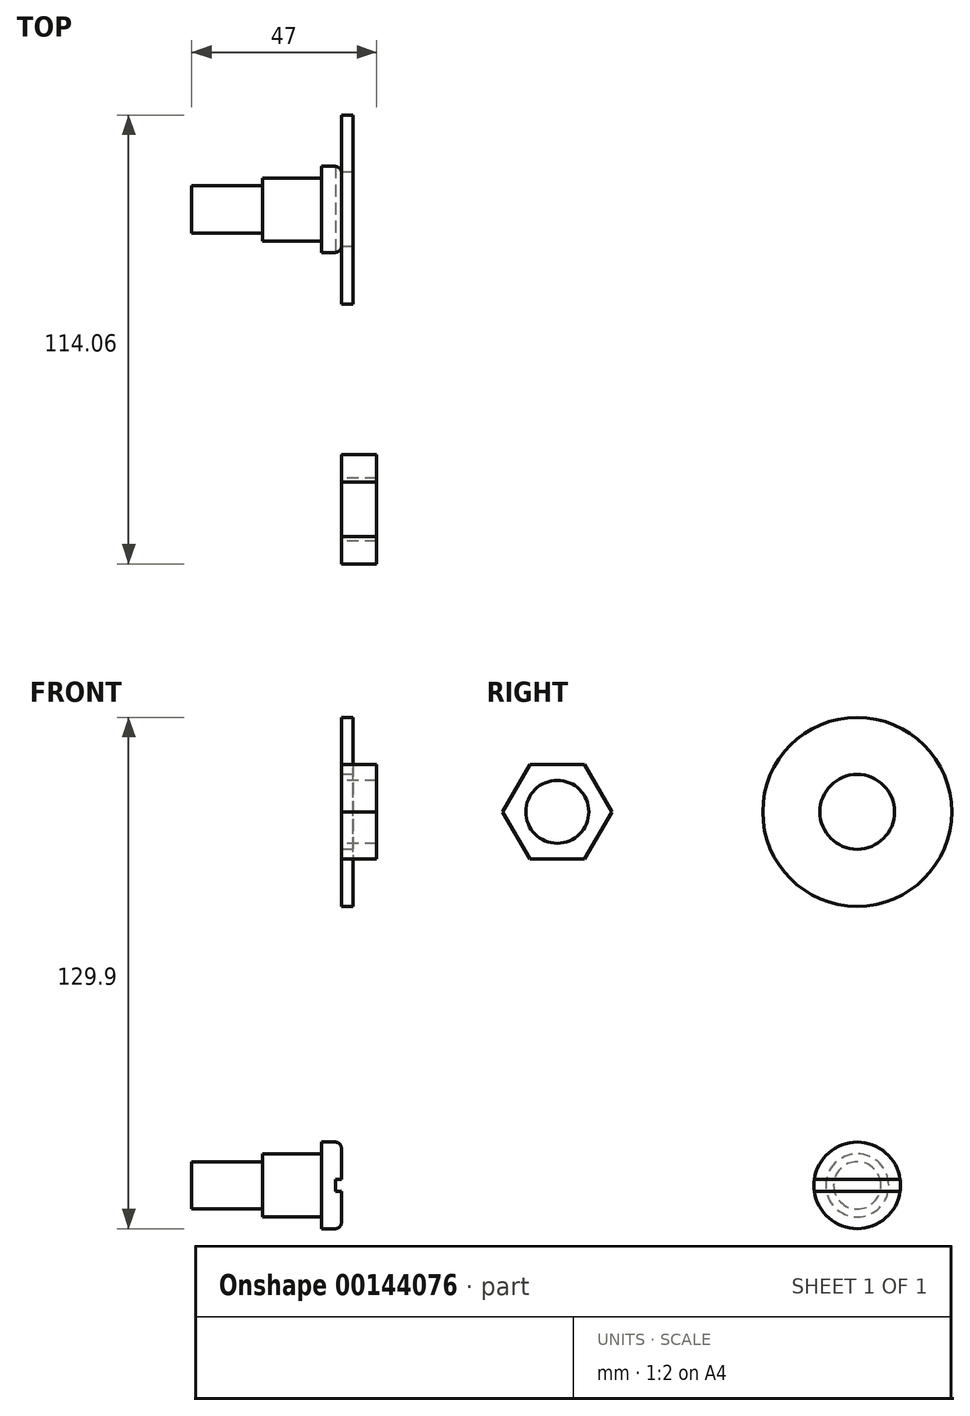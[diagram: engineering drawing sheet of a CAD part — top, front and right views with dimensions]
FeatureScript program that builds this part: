
annotation { "Feature Type Name" : "Feature", "Feature Type Description" : "" }
export const myFeature = defineFeature(function(context is Context, id is Id, definition is map)
    precondition{}
    {
        {
            var Q0;
            Q0=qCreatedBy(makeId("Right.planeOp"),FACE);
            var sketch = newSketch(context, id + "F0", { "sketchPlane" : qUnion([Q0])});
            skCircle(sketch, "E0", {"center": v(38.1, 47.45) * mm, "radius": 24 * mm});
            skCircle(sketch, "E1", {"center": v(38.1, 47.45) * mm, "radius": 9.5 * mm});
            skLineSegment(sketch, "E2", {"start": v(38.1, 47.45) * mm, "end": v(0, 0) * mm, "construction": true});
            skLineSegment(sketch, "E3.MirrorCS", {"start": v(-38.1, 47.45) * mm, "end": v(0, 0) * mm, "construction": true});
            skCircle(sketch, "E4", {"center": v(-38.1, 47.45) * mm, "radius": 8 * mm});
            skLineSegment(sketch, "E5", {"start": v(-45.03, 59.45) * mm, "end": v(-31.17, 59.45) * mm});
            skLineSegment(sketch, "E6", {"start": v(-31.17, 59.45) * mm, "end": v(-24.24, 47.45) * mm});
            skLineSegment(sketch, "E7", {"start": v(-24.24, 47.45) * mm, "end": v(-31.17, 35.45) * mm});
            skLineSegment(sketch, "E8", {"start": v(-31.17, 35.45) * mm, "end": v(-45.03, 35.45) * mm});
            skLineSegment(sketch, "E9", {"start": v(-45.03, 35.45) * mm, "end": v(-51.96, 47.45) * mm});
            skLineSegment(sketch, "E10", {"start": v(-51.96, 47.45) * mm, "end": v(-45.03, 59.45) * mm});
            skLineSegment(sketch, "E11.MirrorCS", {"start": v(38.1, -47.45) * mm, "end": v(0, 0) * mm, "construction": true});
            skCircle(sketch, "E12", {"center": v(38.1, -47.45) * mm, "radius": 11 * mm});
            skCircle(sketch, "E13", {"center": v(38.1, -47.45) * mm, "radius": 8 * mm});
            skCircle(sketch, "E14", {"center": v(38.1, -47.45) * mm, "radius": 6 * mm});
            skSolve(sketch);
        }
        {
            var Q0;
            Q0=makeQuery(id+"F0.imprint","IMPRINT",FACE,{"disambiguationData":[TD([[makeQuery(id+"F0.imprint","IMPRINT",EDGE,{"derivedFrom":sQuery(id+"F0.wireOp",EDGE,"E0")}),1.0]])]});
            extrude(context, id + "F1", {"entities" : qUnion([Q0]), "depth" : 3 * mm});
        }
        {
            var Q0;
            Q0=makeQuery(id+"F0.imprint","IMPRINT",FACE,{"disambiguationData":[TD([[makeQuery(id+"F0.imprint","IMPRINT",EDGE,{"derivedFrom":sQuery(id+"F0.wireOp",EDGE,"E4")}),-1.0]])]});
            extrude(context, id + "F2", {"entities" : qUnion([Q0]), "depth" : 9 * mm});
        }
        {
            var Q0;
            Q0=makeQuery(id+"F0.imprint","IMPRINT",FACE,{"disambiguationData":[TD([[makeQuery(id+"F0.imprint","IMPRINT",EDGE,{"derivedFrom":sQuery(id+"F0.wireOp",EDGE,"E12")}),1.0]])]});
            extrude(context, id + "F3", {"entities" : qUnion([Q0]), "oppositeDirection" : true, "depth" : 5 * mm});
        }
        {
            var Q0;
            Q0=makeQuery(id+"F0.imprint","IMPRINT",FACE,{"disambiguationData":[TD([[makeQuery(id+"F0.imprint","IMPRINT",EDGE,{"derivedFrom":sQuery(id+"F0.wireOp",EDGE,"E13")}),1.0]])]});
            extrude(context, id + "F4", {"entities" : qUnion([Q0]), "operationType" : NewBodyOperationType.ADD, "oppositeDirection" : true, "depth" : 20 * mm});
        }
        {
            var Q0;
            Q0=makeQuery(id+"F0.imprint","IMPRINT",FACE,{"disambiguationData":[TD([[makeQuery(id+"F0.imprint","IMPRINT",EDGE,{"derivedFrom":sQuery(id+"F0.wireOp",EDGE,"E14")}),1.0]])]});
            extrude(context, id + "F5", {"entities" : qUnion([Q0]), "operationType" : NewBodyOperationType.ADD, "oppositeDirection" : true, "depth" : 38 * mm});
        }
        {
            var Q0;
            Q0=makeQuery(id+"F0.imprint","IMPRINT",FACE,{"disambiguationData":[TD([[makeQuery(id+"F0.imprint","IMPRINT",EDGE,{"derivedFrom":sQuery(id+"F0.wireOp",EDGE,"E12")}),1.0]])]});
            var sketch = newSketch(context, id + "F6", { "sketchPlane" : qUnion([Q0])});
            skCircle(sketch, "E15.0", {"center": v(38.1, -47.45) * mm, "radius": 11 * mm});
            skLineSegment(sketch, "E16", {"start": v(49.1, -47.45) * mm, "end": v(27.1, -47.45) * mm, "construction": true});
            skLineSegment(sketch, "E17.0", {"start": v(49, -45.95) * mm, "end": v(27.2, -45.95) * mm});
            skLineSegment(sketch, "E18.0", {"start": v(49, -48.95) * mm, "end": v(27.2, -48.95) * mm});
            skSolve(sketch);
        }
        {
            var Q0;
            {var subQ0=sQuery(id+"F6.wireOp",EDGE,"E17.0");var subQ1=sQuery(id+"F6.wireOp",EDGE,"E15.0");var subQ2=makeQuery(id+"F6.imprint","INTERSECT",VERTEX,{"disambiguationData":[OD(0.0)],"derivedFrom":[subQ1,subQ0]});Q0=makeQuery(id+"F6.imprint","IMPRINT",FACE,{"disambiguationData":[TD([[makeQuery(id+"F6.imprint","IMPRINT",EDGE,{"disambiguationData":[TD([[subQ2,1.0]])],"derivedFrom":subQ1}),1.0]])]});}
            var Q1;
            {var subQ0=sQuery(id+"F6.wireOp",EDGE,"E17.0");var subQ1=makeQuery(id+"F0.imprint","IMPRINT",EDGE,{"derivedFrom":sQuery(id+"F0.wireOp",EDGE,"E13")});var subQ2=makeQuery(id+"F6.imprint","INTERSECT",VERTEX,{"disambiguationData":[OD(0.0)],"derivedFrom":[subQ1,subQ0]});Q1=makeQuery(id+"F6.imprint","IMPRINT",FACE,{"disambiguationData":[TD([[makeQuery(id+"F6.imprint","IMPRINT",EDGE,{"disambiguationData":[TD([[subQ2,-1.0]])],"derivedFrom":subQ0}),1.0]])]});}
            var Q2;
            {var subQ0=sQuery(id+"F6.wireOp",EDGE,"E17.0");var subQ1=sQuery(id+"F6.wireOp",EDGE,"E15.0");var subQ2=makeQuery(id+"F6.imprint","INTERSECT",VERTEX,{"disambiguationData":[OD(1.0)],"derivedFrom":[subQ1,subQ0]});Q2=makeQuery(id+"F6.imprint","IMPRINT",FACE,{"disambiguationData":[TD([[makeQuery(id+"F6.imprint","IMPRINT",EDGE,{"disambiguationData":[TD([[subQ2,-1.0]])],"derivedFrom":subQ1}),1.0]])]});}
            extrude(context, id + "F7", {"entities" : qUnion([Q0, Q1, Q2]), "operationType" : NewBodyOperationType.REMOVE, "oppositeDirection" : true, "depth" : 1.5 * mm});
        }
        {
            var Q0;
            {var subQ2=sQuery(id+"F0.wireOp",EDGE,"E12");Q0=makeQuery(id+"F7.boolean.opBoolean","SPLIT",EDGE,{"disambiguationData":[TD([makeQuery(id+"F7.opExtrude","SWEPT_FACE",FACE,{"disambiguationData":[OSD([sQuery(id+"F6.wireOp",EDGE,"E17.0")])]})])],"derivedFrom":makeQuery(id+"F3.opExtrude","CAP_EDGE",EDGE,{"disambiguationData":[OSD([subQ2])],"isStart":true})});}
            var Q1;
            {var subQ2=sQuery(id+"F0.wireOp",EDGE,"E12");Q1=makeQuery(id+"F7.boolean.opBoolean","SPLIT",EDGE,{"disambiguationData":[TD([makeQuery(id+"F7.opExtrude","SWEPT_FACE",FACE,{"disambiguationData":[OSD([sQuery(id+"F6.wireOp",EDGE,"E18.0")])]})])],"derivedFrom":makeQuery(id+"F3.opExtrude","CAP_EDGE",EDGE,{"disambiguationData":[OSD([subQ2])],"isStart":true})});}
            fillet(context, id + "F8", {"entities" : qUnion([Q0, Q1]), "radius" : 1.5 * mm, "tangentPropagation" : true, "allowEdgeOverflow" : false});
        }
    });
